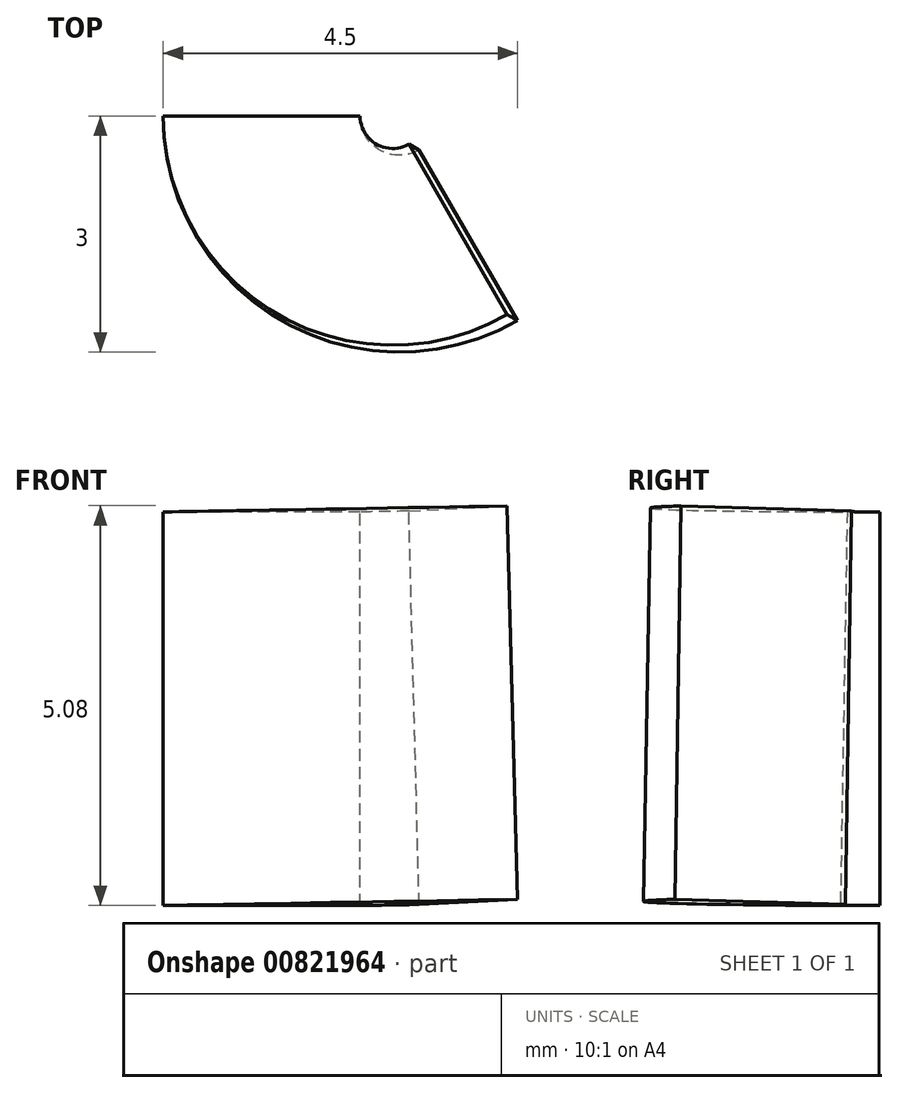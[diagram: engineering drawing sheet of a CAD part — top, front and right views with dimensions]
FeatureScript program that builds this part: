
annotation { "Feature Type Name" : "Feature", "Feature Type Description" : "" }
export const myFeature = defineFeature(function(context is Context, id is Id, definition is map)
    precondition{}
    {
        {
            var Q0;
            Q0=qCreatedBy(makeId("Front.planeOp"),FACE);
            var sketch = newSketch(context, id + "F0", { "sketchPlane" : qUnion([Q0])});
            skLineSegment(sketch, "E0.bottom", {"start": v(0, 0) * mm, "end": v(-2.5, 0) * mm});
            skLineSegment(sketch, "E0.top", {"start": v(0, 5) * mm, "end": v(-2.5, 5) * mm});
            skLineSegment(sketch, "E0.left", {"start": v(0, 0) * mm, "end": v(0, 5) * mm});
            skLineSegment(sketch, "E0.right", {"start": v(-2.5, 0) * mm, "end": v(-2.5, 5) * mm});
            skLineSegment(sketch, "E1", {"start": v(0, 0) * mm, "end": v(0.5, 0) * mm});
            skLineSegment(sketch, "E2", {"start": v(0.5, 0) * mm, "end": v(0, 28.73) * mm});
            skSolve(sketch);
        }
        {
            var Q0;
            Q0=qSketchRegion(id+"F0",true);
            var Q1;
            Q1=sQuery(id+"F0.wireOp",EDGE,"E2");
            revolve(context, id + "F1", {"surfaceOperationType" : NewSurfaceOperationType.NEW, "entities" : qUnion([Q0]), "axis" : qUnion([Q1]), "revolveType" : RevolveType.ONE_DIRECTION, "angle" : 120 * degree});
        }
    });
